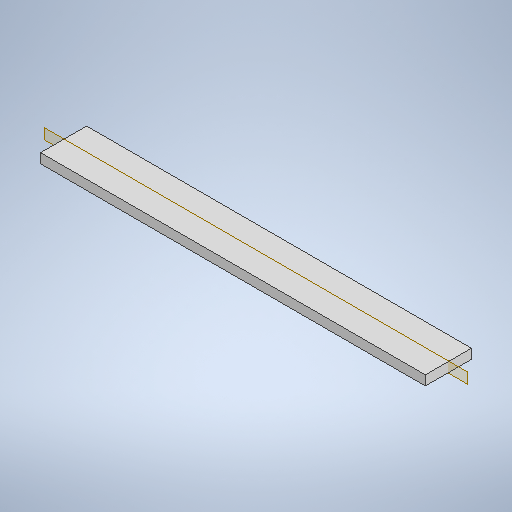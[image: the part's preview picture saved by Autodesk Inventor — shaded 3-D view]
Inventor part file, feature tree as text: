
AUTODESK INVENTOR PART (.ipt)
format: ipt  version: 2025.3 (Build 293356030, 356C)  size: 247,808 bytes
history: native  units: in
note: dims shown in document units (in); Inventor stores cm internally (conversion verified against a paired STEP export)
features: sketch x3, extrude x2, plane x1, revolve x1
ambient origin geometry x8: Origin, YZ Plane, XZ Plane, XY Plane, X Axis, Y Axis, Z Axis, Center Point
bodies: Solid1 (feature_tree)
feature tree (7):
  extrude  "Extrusion1"  Depth=2.5in
  plane  "Work Plane1"
  revolve  "Revolution1"  [1 undecoded]
  extrude  "Extrusion2"  TaperAngle=0.0deg  [1 undecoded]
  sketch  "Sketch1"  dims[d0=0.3in d1=2.5in]
  sketch  "Sketch2"  dims[d2=0.0625in d3=0.0in d4=-0.15in]
  sketch  "Sketch3"  dims[d5=360.0deg d7=0.0in d8=0.0in]
note: 2 required parameter values undecoded (feature->parameter linkage not recoverable at this tier; creation-order binding heuristic only, values carry confidence <= 0.55)